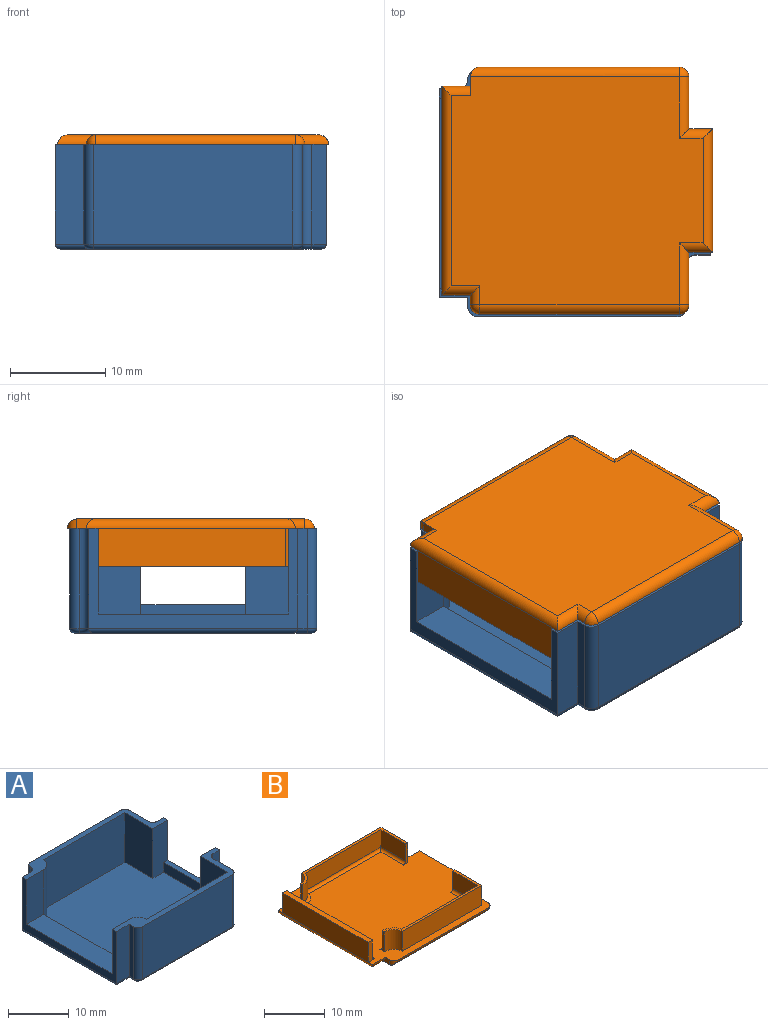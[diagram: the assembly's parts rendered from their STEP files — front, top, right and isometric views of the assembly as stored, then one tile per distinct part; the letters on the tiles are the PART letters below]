
ASSEMBLY  parts=2 mates=1
PART A: 54 faces, bbox 28.5x26.2x11 mm
  f0: plane 24x23.5mm, normal (0,0,1), area 525.2mm2, adj f2,f3,f5,f6,f14,f15,f16,f23
  f1: plane 27.5x25mm, normal (0,0,-1), area 644.2mm2, adj f36,f37,f38,f39,f40,f41,f42,f43
  f2: plane 19x10mm, normal (0,-1,0), area 190mm2, adj f0,f3,f5,f13
  f3: cylinder r=2mm len=10mm, axis (0,0,-1), area 31.4mm2, adj f0,f2,f4,f13,f25
  f4: plane 9x4mm, normal (0,-1,0), area 36mm2, adj f3,f12,f13,f26
  f5: plane 10x6.5mm, normal (-1,0,0), area 65mm2, adj f0,f2,f6,f13
  f6: plane 10x3.5mm, normal (0,-1,0), area 33mm2, adj f0,f5,f7,f13,f34,f35
  f7: plane 13x10.5mm, normal (1,0,0), area 48.5mm2, adj f6,f8,f13,f15,f22,f24,f35,f50
  f8: plane 10.5x1.5mm, normal (0,1,0), area 15.7mm2, adj f7,f13,f33,f52
  f9: plane 10.5x4.5mm, normal (1,0,0), area 47.2mm2, adj f13,f32,f33,f51
  f10: plane 21x10.5mm, normal (0,1,0), area 220.5mm2, adj f13,f30,f32,f47
  f11: plane 10.5x2mm, normal (0,1,0), area 21mm2, adj f12,f13,f31,f41
  f12: plane 22x10.5mm, normal (-1,0,0), area 51mm2, adj f4,f11,f13,f17,f18,f24,f26,f39
  f13: plane 28.5x7.5mm, normal (0,0,1), area 40.1mm2, adj f2,f3,f4,f5,f6,f7,f8,f9
  f14: plane 19x10mm, normal (0,1,0), area 190mm2, adj f0,f16,f23,f24
  f15: plane 10x3.5mm, normal (0,1,0), area 33mm2, adj f0,f7,f23,f24,f34,f35
  f16: cylinder r=2mm len=10mm, axis (0,0,-1), area 31.4mm2, adj f0,f14,f17,f24,f25
  f17: plane 9x4mm, normal (0,1,0), area 36mm2, adj f12,f16,f24,f26
  f18: plane 10.5x3mm, normal (0,-1,0), area 31.5mm2, adj f12,f19,f24,f37
  f19: plane 10.5x1mm, normal (-1,0,0), area 10.5mm2, adj f18,f24,f27,f36
  f20: plane 21x10.5mm, normal (0,-1,0), area 220.5mm2, adj f24,f27,f28,f40
  f21: plane 10.5x4.5mm, normal (1,0,0), area 47.2mm2, adj f24,f28,f29,f44
  f22: plane 10.5x1.5mm, normal (0,-1,0), area 15.7mm2, adj f7,f24,f29,f48
  f23: plane 10x6.5mm, normal (-1,0,0), area 65mm2, adj f0,f14,f15,f24
  f24: plane 28.5x7.5mm, normal (0,0,1), area 39.9mm2, adj f7,f12,f14,f15,f16,f17,f18,f19
  f25: plane 20x1mm, normal (1,0,0), area 20mm2, adj f0,f3,f16,f26
  f26: plane 20x4mm, normal (0,0,1), area 80mm2, adj f4,f12,f17,f25
  f27: cylinder r=1mm len=10.5mm, axis (0,0,1), area 16.5mm2, adj f19,f20,f24,f38
  f28: cylinder r=1mm len=10.5mm, axis (0,0,-1), area 16.5mm2, adj f20,f21,f24,f42
  f29: cylinder r=1mm len=10.5mm, axis (0,0,1), area 16.5mm2, adj f21,f22,f24,f46
  f30: cylinder r=1mm len=10.5mm, axis (0,0,-1), area 16.5mm2, adj f10,f13,f31,f45
  f31: cylinder r=1mm len=10.5mm, axis (0,0,1), area 16.5mm2, adj f11,f13,f30,f43
  f32: cylinder r=1mm len=10.5mm, axis (0,0,1), area 16.5mm2, adj f9,f10,f13,f49
  f33: cylinder r=1mm len=10.5mm, axis (0,0,-1), area 16.5mm2, adj f8,f9,f13,f53
  f34: plane 11x2mm, normal (-1,0,0), area 22mm2, adj f0,f6,f15,f35
  f35: plane 11x1mm, normal (0,0,1), area 11mm2, adj f6,f7,f15,f34
  f36: cylinder r=0.5mm len=1.5mm, axis (0,-1,0), area 0.9mm2, adj f1,f19,f37,f38
  f37: cylinder r=0.5mm len=3.5mm, axis (1,0,0), area 2.4mm2, adj f1,f18,f36,f39
  f38: torus R=0.5mm, axis (0,0,1), area 1mm2, adj f1,f27,f36,f40
  f39: cylinder r=0.5mm len=22mm, axis (0,-1,0), area 17mm2, adj f1,f12,f37,f41
  f40: cylinder r=0.5mm len=21mm, axis (1,0,0), area 16.5mm2, adj f1,f20,f38,f42
  f41: cylinder r=0.5mm len=2mm, axis (-1,0,0), area 1.4mm2, adj f1,f11,f39,f43
  f42: torus R=0.5mm, axis (0,0,1), area 1mm2, adj f1,f28,f40,f44
  f43: torus R=1.5mm, axis (0,0,1), area 1.5mm2, adj f1,f31,f41,f45
  f44: cylinder r=0.5mm len=4.5mm, axis (0,1,0), area 3.5mm2, adj f1,f21,f42,f46
  f45: torus R=0.5mm, axis (0,0,1), area 1mm2, adj f1,f30,f43,f47
  f46: torus R=1.5mm, axis (0,0,1), area 1.5mm2, adj f1,f29,f44,f48
  f47: cylinder r=0.5mm len=21mm, axis (-1,0,0), area 16.5mm2, adj f1,f10,f45,f49
  f48: cylinder r=0.5mm len=1.5mm, axis (1,0,0), area 1mm2, adj f1,f22,f46,f50
  f49: torus R=0.5mm, axis (0,0,1), area 1mm2, adj f1,f32,f47,f51
  f50: cylinder r=0.5mm len=13mm, axis (0,1,0), area 9.9mm2, adj f1,f7,f48,f52
  f51: cylinder r=0.5mm len=4.5mm, axis (0,1,0), area 3.5mm2, adj f1,f9,f49,f53
  f52: cylinder r=0.5mm len=1.5mm, axis (-1,0,0), area 1mm2, adj f1,f8,f50,f53
  f53: torus R=1.5mm, axis (0,0,1), area 1.5mm2, adj f1,f33,f51,f52
PART B: 48 faces, bbox 28.5x26x5 mm
  f0: plane 20x4mm, normal (-1,0,0), area 80mm2, adj f23,f24,f25,f30
  f1: plane 2x1mm, normal (-1,0,0), area 1.2mm2, adj f2,f3,f26,f28
  f2: plane 28.5x26mm, normal (0,0,1), area 611.8mm2, adj f1,f5,f6,f7,f10,f11,f15,f16
  f3: plane 26.5x24mm, normal (0,0,-1), area 593.5mm2, adj f1,f27,f28,f30,f31,f32,f33,f34
  f4: plane 20.75x6.25mm, normal (0,0,1), area 13.7mm2, adj f5,f6,f7,f8,f9,f10,f11,f12
  f5: plane 18.51x4mm, normal (0,1,0), area 74.1mm2, adj f2,f4,f6,f11
  f6: plane 6.25x4mm, normal (1,0,0), area 25mm2, adj f2,f4,f5,f7
  f7: plane 4x1mm, normal (0,-1,0), area 2.1mm2, adj f2,f4,f6,f8,f44
  f8: plane 5.75x3.5mm, normal (-1,0,0), area 20.1mm2, adj f4,f7,f12,f44
  f9: cylinder r=2.75mm len=3.5mm, axis (0,0,-1), area 12.5mm2, adj f4,f10,f12,f46
  f10: plane 4x1mm, normal (-1,0,0), area 2.1mm2, adj f2,f4,f9,f11,f46
  f11: cylinder r=2.25mm len=4mm, axis (0,0,-1), area 13.1mm2, adj f2,f4,f5,f10
  f12: plane 17.6x3.5mm, normal (0,-1,0), area 61.6mm2, adj f4,f8,f9,f45
  f13: plane 20.75x6.25mm, normal (0,0,1), area 13.7mm2, adj f14,f15,f16,f17,f18,f19,f20,f21
  f14: plane 5.75x3.5mm, normal (-1,0,0), area 20.1mm2, adj f13,f15,f21,f43
  f15: plane 4x1mm, normal (0,1,0), area 2.1mm2, adj f2,f13,f14,f16,f43
  f16: plane 6.25x4mm, normal (1,0,0), area 25mm2, adj f2,f13,f15,f17
  f17: plane 18.51x4mm, normal (0,-1,0), area 74.1mm2, adj f2,f13,f16,f18
  f18: cylinder r=2.25mm len=4mm, axis (0,0,-1), area 13.1mm2, adj f2,f13,f17,f19
  f19: plane 4x1mm, normal (-1,0,0), area 2.1mm2, adj f2,f13,f18,f20,f41
  f20: cylinder r=2.75mm len=3.5mm, axis (0,0,-1), area 12.5mm2, adj f13,f19,f21,f41
  f21: plane 17.6x3.5mm, normal (0,1,0), area 61.6mm2, adj f13,f14,f20,f42
  f22: plane 20x3.5mm, normal (1,0,0), area 70mm2, adj f23,f24,f25,f47
  f23: plane 4x1.5mm, normal (0,1,0), area 4.1mm2, adj f0,f2,f22,f25,f47
  f24: plane 4x1.5mm, normal (0,-1,0), area 4.1mm2, adj f0,f2,f22,f25,f47
  f25: plane 20x1mm, normal (0,0,1), area 20mm2, adj f0,f22,f23,f24
  f26: cylinder r=1mm len=1mm, axis (0,0,1), area 1mm2, adj f1,f2,f27
  f27: cylinder r=1mm len=22mm, axis (1,0,0), area 34mm2, adj f2,f3,f26,f29
  f28: cylinder r=1mm len=3mm, axis (1,0,0), area 4.1mm2, adj f1,f2,f3,f30
  f29: sphere r=1mm, area 1.6mm2, adj f2,f27,f31
  f30: cylinder r=1mm len=22mm, axis (0,-1,0), area 33.4mm2, adj f0,f2,f3,f28,f32
  f31: cylinder r=1mm len=6.5mm, axis (0,1,0), area 9.2mm2, adj f2,f3,f29,f33
  f32: cylinder r=1mm len=4mm, axis (-1,0,0), area 4.7mm2, adj f2,f3,f30,f34
  f33: cylinder r=1mm len=3.5mm, axis (1,0,0), area 3.9mm2, adj f2,f3,f31,f35
  f34: cylinder r=1mm len=2mm, axis (0,-1,0), area 2.1mm2, adj f2,f3,f32,f36
  f35: cylinder r=1mm len=13mm, axis (0,1,0), area 19.3mm2, adj f2,f3,f33,f37
  f36: sphere r=1mm, area 1.6mm2, adj f2,f34,f38
  f37: cylinder r=1mm len=3.5mm, axis (-1,0,0), area 3.9mm2, adj f2,f3,f35,f39
  f38: cylinder r=1mm len=21mm, axis (-1,0,0), area 33mm2, adj f2,f3,f36,f40
  f39: cylinder r=1mm len=6.5mm, axis (0,1,0), area 9.2mm2, adj f2,f3,f37,f40
  f40: sphere r=1mm, area 1.6mm2, adj f2,f38,f39
  f41: torus R=3.25mm, axis (0,0,1), area 2.9mm2, adj f2,f19,f20,f42
  f42: cylinder r=0.5mm len=17.6mm, axis (-1,0,0), area 13.6mm2, adj f2,f21,f41,f43
  f43: cylinder r=0.5mm len=5.75mm, axis (0,-1,0), area 4.4mm2, adj f2,f14,f15,f42
  f44: cylinder r=0.5mm len=5.75mm, axis (0,-1,0), area 4.4mm2, adj f2,f7,f8,f45
  f45: cylinder r=0.5mm len=17.6mm, axis (1,0,0), area 13.6mm2, adj f2,f12,f44,f46
  f46: torus R=3.25mm, axis (0,0,1), area 2.9mm2, adj f2,f9,f10,f45
  f47: cylinder r=0.5mm len=20mm, axis (0,1,0), area 15.7mm2, adj f2,f22,f23,f24
PLACE A t=(2.25,4.68,-2.7)mm
PLACE B rot(axis=(1,0,0),180deg) t=(2.5,4.93,9.3)mm
MATE fastened B.f2 <-> A.f32  axis (0,0,-1) through (12.75,16.68,8.3)mm
